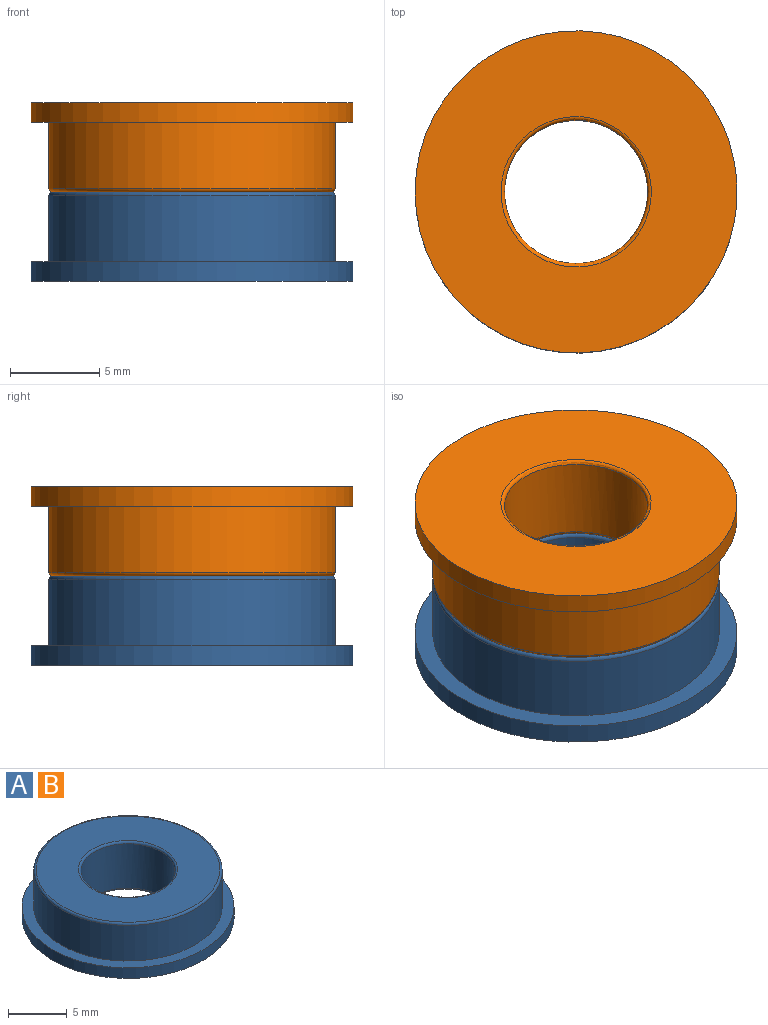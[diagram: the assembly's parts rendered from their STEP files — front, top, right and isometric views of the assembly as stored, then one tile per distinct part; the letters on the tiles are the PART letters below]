
ASSEMBLY  parts=2 mates=1
PART A: 9 faces, bbox 18x18x5 mm
  f0: plane 18x18mm, normal (0,0,-1), area 199.1mm2, adj f1,f8
  f1: cylinder r=9mm len=18mm, axis (0,0,-1), area 62.2mm2, adj f0,f2
  f2: plane 18x18mm, normal (0,0,1), area 53.4mm2, adj f1,f3
  f3: cylinder r=8mm len=16mm, axis (0,0,-1), area 186mm2, adj f2,f6
  f4: plane 15.6x15.6mm, normal (0,0,1), area 135.7mm2, adj f6,f7
  f5: cylinder r=4mm len=8mm, axis (0,0,-1), area 115.6mm2, adj f7,f8
  f6: torus R=7.8mm, axis (0,0,-1), area 15.6mm2, adj f3,f4
  f7: torus R=4.2mm, axis (0,0,-1), area 8mm2, adj f4,f5
  f8: torus R=4.2mm, axis (0,0,1), area 8mm2, adj f0,f5
PART B: same geometry as A
PLACE A t=(0,0,-5)mm
PLACE B rot(axis=(1,0,0),180deg) t=(0,0,5)mm
MATE fastened B.f1 <-> A.f1  axis (0,0,-1) through (0,0,0)mm
